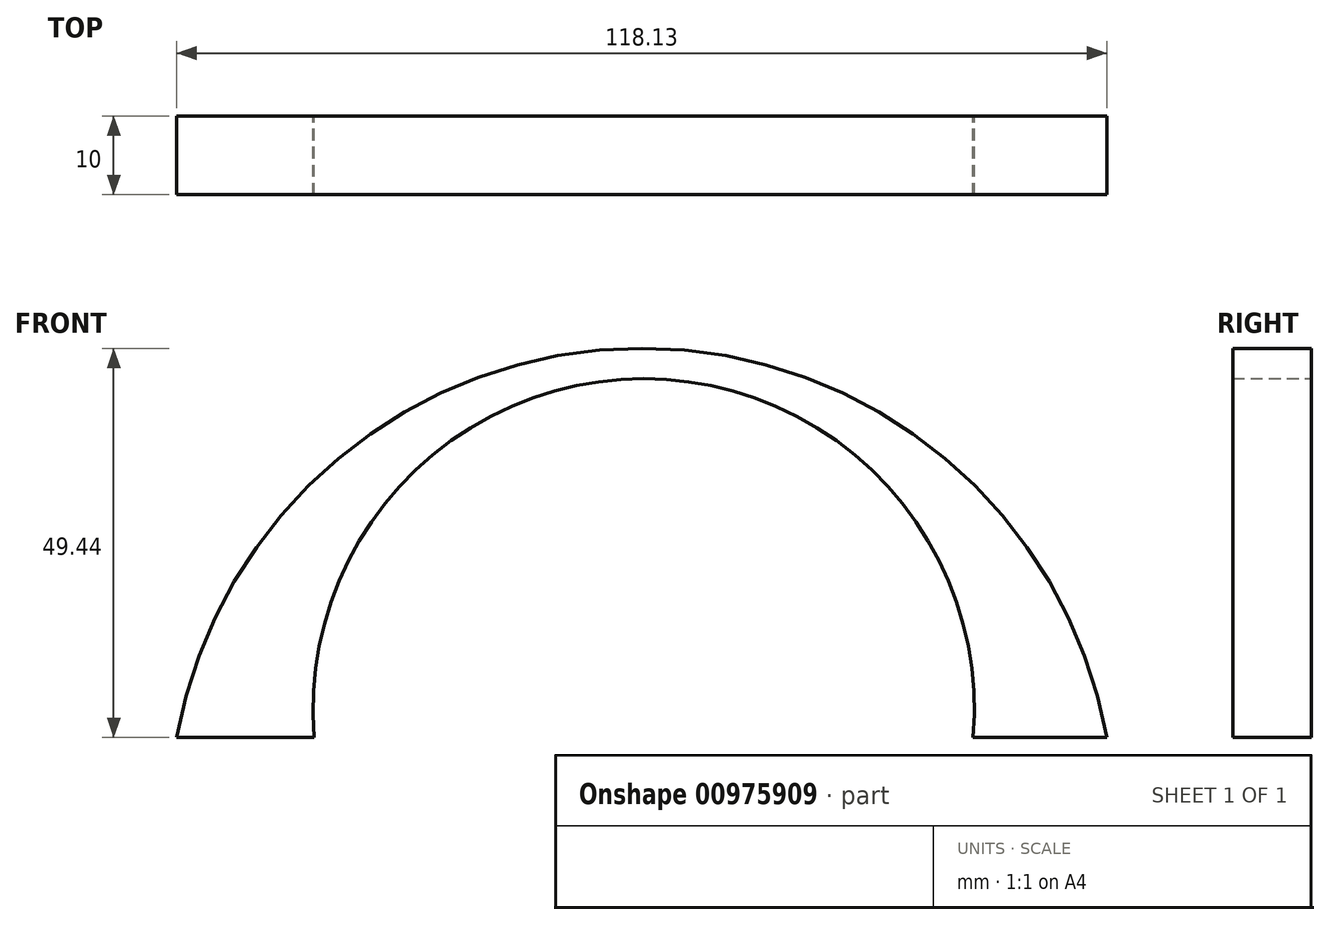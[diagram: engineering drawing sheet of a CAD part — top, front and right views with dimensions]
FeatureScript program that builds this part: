
annotation { "Feature Type Name" : "Feature", "Feature Type Description" : "" }
export const myFeature = defineFeature(function(context is Context, id is Id, definition is map)
    precondition{}
    {
        {
            var Q0;
            Q0=qCreatedBy(makeId("Front.planeOp"),FACE);
            var sketch = newSketch(context, id + "F0", { "sketchPlane" : qUnion([Q0])});
            skArc(sketch, "E0", {"start": v(65.41, 0) * mm, "mid": v(6.35, 49.44) * mm, "end": v(-52.72, 0) * mm});
            skArc(sketch, "E1", {"start": v(48.44, 0) * mm, "mid": v(6.6, 45.58) * mm, "end": v(-35.25, 0) * mm});
            skLineSegment(sketch, "E2", {"start": v(-52.72, 0) * mm, "end": v(-35.25, 0) * mm});
            skLineSegment(sketch, "E3", {"start": v(48.44, 0) * mm, "end": v(65.41, 0) * mm});
            skSolve(sketch);
        }
        {
            var Q0;
            Q0=makeQuery(id+"F0.imprint","IMPRINT",FACE,{"disambiguationData":[TD([[makeQuery(id+"F0.imprint","IMPRINT",EDGE,{"derivedFrom":sQuery(id+"F0.wireOp",EDGE,"E0")}),1.0]])]});
            extrude(context, id + "F1", {"entities" : qUnion([Q0]), "depth" : 10 * mm, "offsetDistance" : 25 * mm});
        }
    });
